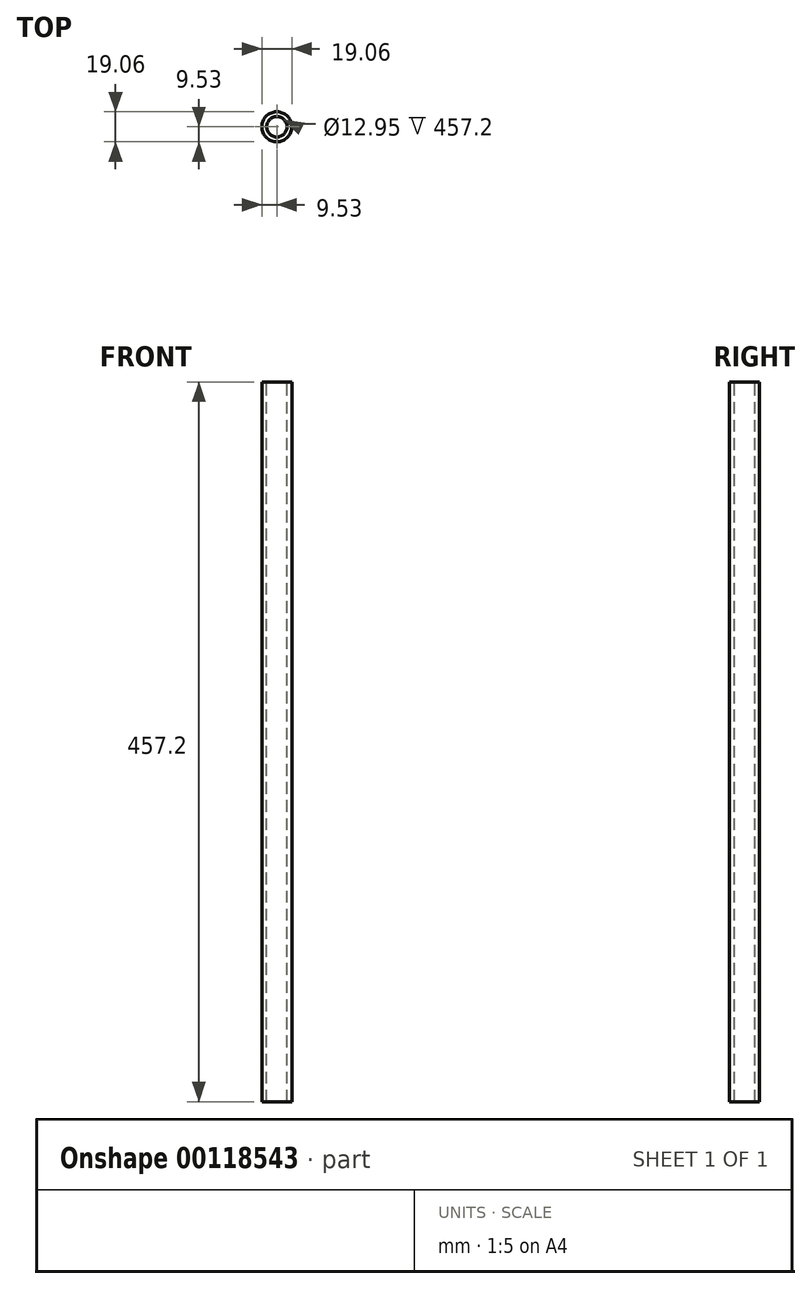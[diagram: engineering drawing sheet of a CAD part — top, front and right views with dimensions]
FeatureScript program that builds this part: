
annotation { "Feature Type Name" : "Feature", "Feature Type Description" : "" }
export const myFeature = defineFeature(function(context is Context, id is Id, definition is map)
    precondition{}
    {
        {
            var Q0;
            Q0=qCreatedBy(makeId("Top.planeOp"),FACE);
            var sketch = newSketch(context, id + "F0", { "sketchPlane" : qUnion([Q0])});
            skCircle(sketch, "E0", {"center": v(0, 0) * mm, "radius": 9.53 * mm});
            skSolve(sketch);
        }
        {
            var Q0;
            Q0=makeQuery(id+"F0.imprint","IMPRINT",FACE,{"disambiguationData":[TD([[makeQuery(id+"F0.imprint","IMPRINT",EDGE,{"derivedFrom":sQuery(id+"F0.wireOp",EDGE,"E0")}),1.0]])]});
            extrude(context, id + "F1", {"entities" : qUnion([Q0]), "depth" : 457.2 * mm});
        }
        {
            var Q0;
            Q0=makeQuery(id+"F1.opExtrude","CAP_FACE",FACE,{"disambiguationData":[OSD([sQuery(id+"F0.wireOp",EDGE,"E0")])],"isStart":false});
            var sketch = newSketch(context, id + "F2", { "sketchPlane" : qUnion([Q0])});
            skCircle(sketch, "E1", {"center": v(0, 0) * mm, "radius": 6.48 * mm});
            skSolve(sketch);
        }
        {
            var Q0;
            Q0=makeQuery(id+"F2.imprint","IMPRINT",FACE,{"disambiguationData":[TD([[makeQuery(id+"F2.imprint","IMPRINT",EDGE,{"derivedFrom":sQuery(id+"F2.wireOp",EDGE,"E1")}),1.0]])]});
            extrude(context, id + "F3", {"entities" : qUnion([Q0]), "operationType" : NewBodyOperationType.REMOVE, "endBound" : BoundingType.UP_TO_NEXT, "oppositeDirection" : true, "depth" : 25.4 * mm});
        }
    });
